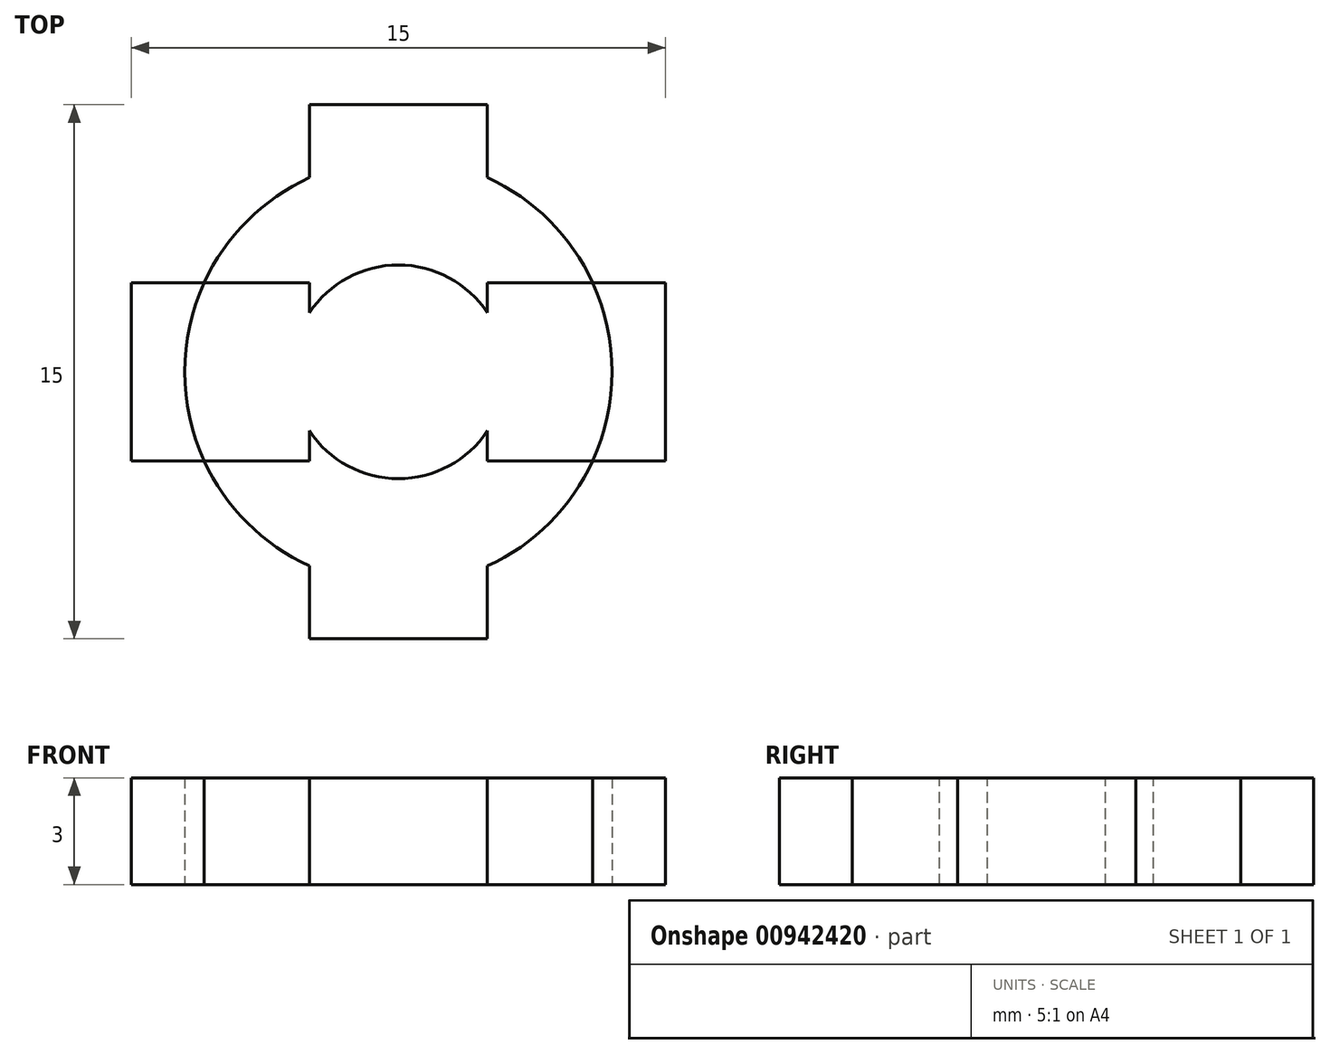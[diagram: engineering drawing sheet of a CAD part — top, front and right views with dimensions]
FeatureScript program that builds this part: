
annotation { "Feature Type Name" : "Feature", "Feature Type Description" : "" }
export const myFeature = defineFeature(function(context is Context, id is Id, definition is map)
    precondition{}
    {
        {
            var Q0;
            Q0=qCreatedBy(makeId("Top.planeOp"),FACE);
            var sketch = newSketch(context, id + "F0", { "sketchPlane" : qUnion([Q0])});
            skCircle(sketch, "E0.0", {"center": v(0, 0) * mm, "radius": 5.5 * mm, "construction": true});
            skCircle(sketch, "E1", {"center": v(0, 0) * mm, "radius": 6 * mm});
            skLineSegment(sketch, "E2", {"start": v(0, 13.29) * mm, "end": v(0, -11.87) * mm, "construction": true});
            skLineSegment(sketch, "E3", {"start": v(-2.5, 7.5) * mm, "end": v(2.5, 7.5) * mm});
            skLineSegment(sketch, "E4", {"start": v(2.5, 7.5) * mm, "end": v(2.5, -7.5) * mm});
            skLineSegment(sketch, "E5", {"start": v(2.5, -7.5) * mm, "end": v(-2.5, -7.5) * mm});
            skLineSegment(sketch, "E6", {"start": v(-2.5, -7.5) * mm, "end": v(-2.5, 7.5) * mm});
            skLineSegment(sketch, "E7", {"start": v(7.5, 2.5) * mm, "end": v(7.5, -2.5) * mm});
            skLineSegment(sketch, "E8", {"start": v(7.5, -2.5) * mm, "end": v(-7.5, -2.5) * mm});
            skLineSegment(sketch, "E9", {"start": v(-7.5, -2.5) * mm, "end": v(-7.5, 2.5) * mm});
            skLineSegment(sketch, "E10", {"start": v(-7.5, 2.5) * mm, "end": v(7.5, 2.5) * mm});
            skLineSegment(sketch, "E11", {"start": v(13.83, 0) * mm, "end": v(-10.1, 0) * mm, "construction": true});
            skSolve(sketch);
        }
        {
            var Q0;
            {var subQ0=sQuery(id+"F0.wireOp",EDGE,"E4");var subQ1=sQuery(id+"F0.wireOp",EDGE,"E1");var subQ2=makeQuery(id+"F0.imprint","INTERSECT",VERTEX,{"disambiguationData":[OD(0.0)],"derivedFrom":[subQ1,subQ0]});Q0=makeQuery(id+"F0.imprint","IMPRINT",FACE,{"disambiguationData":[TD([[makeQuery(id+"F0.imprint","IMPRINT",EDGE,{"disambiguationData":[TD([[subQ2,1.0]])],"derivedFrom":subQ1}),1.0]])]});}
            var Q1;
            {var subQ5=sQuery(id+"F0.wireOp",EDGE,"E5");Q1=makeQuery(id+"F0.imprint","IMPRINT",FACE,{"disambiguationData":[TD([[makeQuery(id+"F0.imprint","IMPRINT",EDGE,{"derivedFrom":subQ5}),-1.0]])]});}
            var Q2;
            {var subQ0=sQuery(id+"F0.wireOp",EDGE,"E8");var subQ1=sQuery(id+"F0.wireOp",EDGE,"E1");var subQ2=makeQuery(id+"F0.imprint","INTERSECT",VERTEX,{"disambiguationData":[OD(0.0)],"derivedFrom":[subQ1,subQ0]});Q2=makeQuery(id+"F0.imprint","IMPRINT",FACE,{"disambiguationData":[TD([[makeQuery(id+"F0.imprint","IMPRINT",EDGE,{"disambiguationData":[TD([[subQ2,-1.0]])],"derivedFrom":subQ1}),1.0]])]});}
            var Q3;
            {var subQ5=sQuery(id+"F0.wireOp",EDGE,"E9");Q3=makeQuery(id+"F0.imprint","IMPRINT",FACE,{"disambiguationData":[TD([[makeQuery(id+"F0.imprint","IMPRINT",EDGE,{"derivedFrom":subQ5}),-1.0]])]});}
            var Q4;
            {var subQ0=sQuery(id+"F0.wireOp",EDGE,"E4");var subQ1=sQuery(id+"F0.wireOp",EDGE,"E1");var subQ2=makeQuery(id+"F0.imprint","INTERSECT",VERTEX,{"disambiguationData":[OD(1.0)],"derivedFrom":[subQ1,subQ0]});Q4=makeQuery(id+"F0.imprint","IMPRINT",FACE,{"disambiguationData":[TD([[makeQuery(id+"F0.imprint","IMPRINT",EDGE,{"disambiguationData":[TD([[subQ2,-1.0]])],"derivedFrom":subQ1}),1.0]])]});}
            var Q5;
            {var subQ0=sQuery(id+"F0.wireOp",EDGE,"E6");var subQ1=sQuery(id+"F0.wireOp",EDGE,"E1");var subQ2=makeQuery(id+"F0.imprint","INTERSECT",VERTEX,{"disambiguationData":[OD(0.0)],"derivedFrom":[subQ1,subQ0]});Q5=makeQuery(id+"F0.imprint","IMPRINT",FACE,{"disambiguationData":[TD([[makeQuery(id+"F0.imprint","IMPRINT",EDGE,{"disambiguationData":[TD([[subQ2,-1.0]])],"derivedFrom":subQ1}),1.0]])]});}
            var Q6;
            {var subQ0=sQuery(id+"F0.wireOp",EDGE,"E10");var subQ1=sQuery(id+"F0.wireOp",EDGE,"E1");var subQ2=makeQuery(id+"F0.imprint","INTERSECT",VERTEX,{"disambiguationData":[OD(0.0)],"derivedFrom":[subQ1,subQ0]});Q6=makeQuery(id+"F0.imprint","IMPRINT",FACE,{"disambiguationData":[TD([[makeQuery(id+"F0.imprint","IMPRINT",EDGE,{"disambiguationData":[TD([[subQ2,1.0]])],"derivedFrom":subQ1}),1.0]])]});}
            var Q7;
            {var subQ0=sQuery(id+"F0.wireOp",EDGE,"E10");var subQ1=sQuery(id+"F0.wireOp",EDGE,"E4");var subQ2=makeQuery(id+"F0.imprint","INTERSECT",VERTEX,{"derivedFrom":[subQ1,subQ0]});Q7=makeQuery(id+"F0.imprint","IMPRINT",FACE,{"disambiguationData":[TD([[makeQuery(id+"F0.imprint","IMPRINT",EDGE,{"disambiguationData":[TD([[subQ2,-1.0]])],"derivedFrom":subQ1}),-1.0]])]});}
            var Q8;
            {var subQ0=sQuery(id+"F0.wireOp",EDGE,"E10");var subQ1=sQuery(id+"F0.wireOp",EDGE,"E1");var subQ2=makeQuery(id+"F0.imprint","INTERSECT",VERTEX,{"disambiguationData":[OD(1.0)],"derivedFrom":[subQ1,subQ0]});Q8=makeQuery(id+"F0.imprint","IMPRINT",FACE,{"disambiguationData":[TD([[makeQuery(id+"F0.imprint","IMPRINT",EDGE,{"disambiguationData":[TD([[subQ2,-1.0]])],"derivedFrom":subQ1}),1.0]])]});}
            var Q9;
            {var subQ0=sQuery(id+"F0.wireOp",EDGE,"E4");var subQ1=sQuery(id+"F0.wireOp",EDGE,"E1");var subQ2=makeQuery(id+"F0.imprint","INTERSECT",VERTEX,{"disambiguationData":[OD(0.0)],"derivedFrom":[subQ1,subQ0]});Q9=makeQuery(id+"F0.imprint","IMPRINT",FACE,{"disambiguationData":[TD([[makeQuery(id+"F0.imprint","IMPRINT",EDGE,{"disambiguationData":[TD([[subQ2,-1.0]])],"derivedFrom":subQ1}),1.0]])]});}
            var Q10;
            {var subQ5=sQuery(id+"F0.wireOp",EDGE,"E3");Q10=makeQuery(id+"F0.imprint","IMPRINT",FACE,{"disambiguationData":[TD([[makeQuery(id+"F0.imprint","IMPRINT",EDGE,{"derivedFrom":subQ5}),-1.0]])]});}
            var Q11;
            {var subQ5=sQuery(id+"F0.wireOp",EDGE,"E7");Q11=makeQuery(id+"F0.imprint","IMPRINT",FACE,{"disambiguationData":[TD([[makeQuery(id+"F0.imprint","IMPRINT",EDGE,{"derivedFrom":subQ5}),-1.0]])]});}
            var Q12;
            {var subQ0=sQuery(id+"F0.wireOp",EDGE,"E6");var subQ1=sQuery(id+"F0.wireOp",EDGE,"E1");var subQ2=makeQuery(id+"F0.imprint","INTERSECT",VERTEX,{"disambiguationData":[OD(1.0)],"derivedFrom":[subQ1,subQ0]});Q12=makeQuery(id+"F0.imprint","IMPRINT",FACE,{"disambiguationData":[TD([[makeQuery(id+"F0.imprint","IMPRINT",EDGE,{"disambiguationData":[TD([[subQ2,-1.0]])],"derivedFrom":subQ1}),1.0]])]});}
            extrude(context, id + "F1", {"entities" : qUnion([Q0, Q1, Q2, Q3, Q4, Q5, Q6, Q7, Q8, Q9, Q10, Q11, Q12]), "depth" : 3 * mm, "offsetDistance" : 25 * mm});
        }
        {
            var Q0;
            Q0=makeQuery(id+"F1.opExtrude","CAP_FACE",FACE,{"disambiguationData":[OSD([sQuery(id+"F0.wireOp",EDGE,"E1"),sQuery(id+"F0.wireOp",EDGE,"E3"),sQuery(id+"F0.wireOp",EDGE,"E4"),sQuery(id+"F0.wireOp",EDGE,"E5"),sQuery(id+"F0.wireOp",EDGE,"E6"),sQuery(id+"F0.wireOp",EDGE,"E7"),sQuery(id+"F0.wireOp",EDGE,"E8"),sQuery(id+"F0.wireOp",EDGE,"E9"),sQuery(id+"F0.wireOp",EDGE,"E10")])],"isStart":false});
            var sketch = newSketch(context, id + "F2", { "sketchPlane" : qUnion([Q0])});
            skCircle(sketch, "E12", {"center": v(0, 0) * mm, "radius": 3 * mm});
            skSolve(sketch);
        }
        {
            var Q0;
            Q0=makeQuery(id+"F2.imprint","IMPRINT",FACE,{"disambiguationData":[TD([[makeQuery(id+"F2.imprint","IMPRINT",EDGE,{"derivedFrom":sQuery(id+"F2.wireOp",EDGE,"E12")}),1.0]])]});
            extrude(context, id + "F3", {"entities" : qUnion([Q0]), "operationType" : NewBodyOperationType.REMOVE, "oppositeDirection" : true, "depth" : 25 * mm, "offsetDistance" : 25 * mm});
        }
    });
